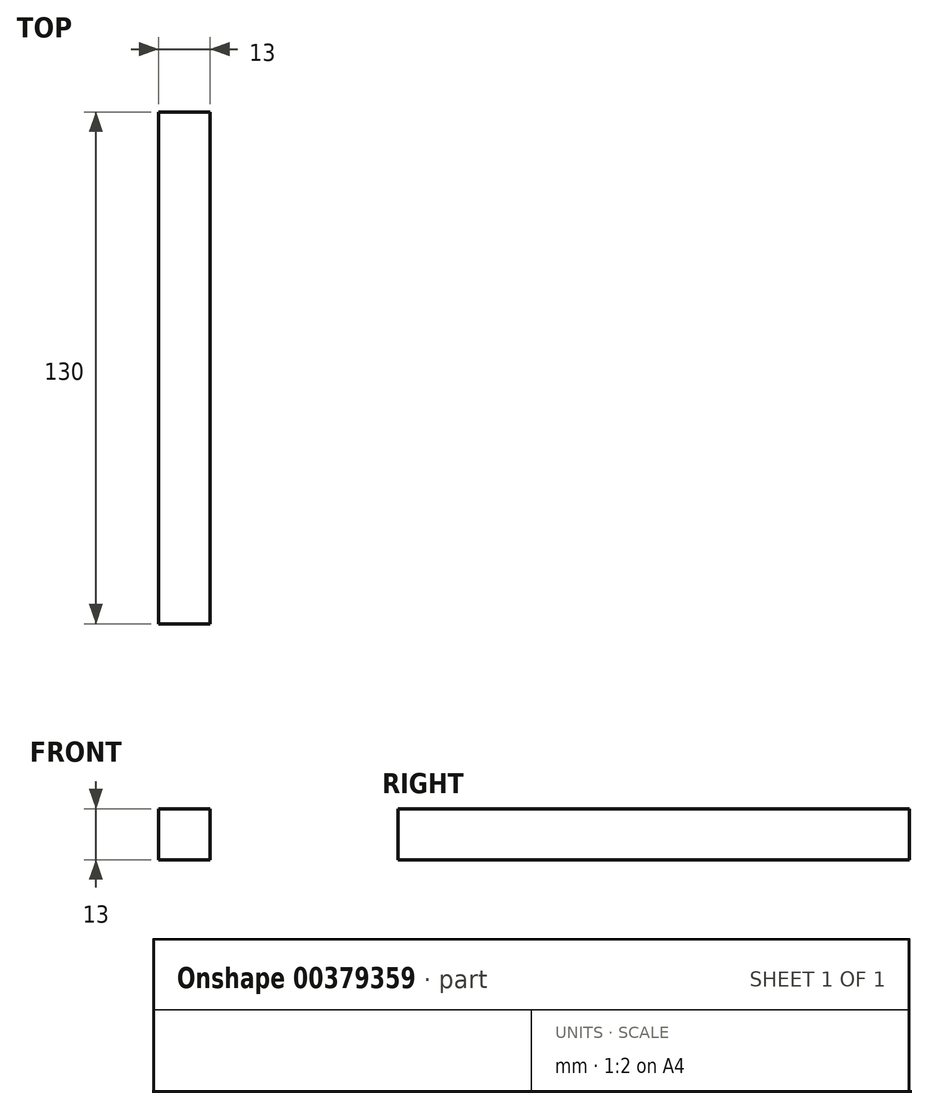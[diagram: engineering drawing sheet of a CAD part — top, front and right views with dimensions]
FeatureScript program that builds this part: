
annotation { "Feature Type Name" : "Feature", "Feature Type Description" : "" }
export const myFeature = defineFeature(function(context is Context, id is Id, definition is map)
    precondition{}
    {
        {
            var Q0;
            Q0=qCreatedBy(makeId("Front.planeOp"),FACE);
            var sketch = newSketch(context, id + "F0", { "sketchPlane" : qUnion([Q0])});
            skLineSegment(sketch, "E0.bottom", {"start": v(-45, 25.71) * mm, "end": v(-32, 25.71) * mm});
            skLineSegment(sketch, "E0.top", {"start": v(-45, 12.71) * mm, "end": v(-32, 12.71) * mm});
            skLineSegment(sketch, "E0.left", {"start": v(-45, 25.71) * mm, "end": v(-45, 12.71) * mm});
            skLineSegment(sketch, "E0.right", {"start": v(-32, 25.71) * mm, "end": v(-32, 12.71) * mm});
            skSolve(sketch);
        }
        {
            var Q0;
            Q0 = qSketchRegion(id + "F0", true);
            extrude(context, id + "F1", {"entities" : qUnion([Q0]), "depth" : 130 * mm, "offsetDistance" : 25 * mm});
        }
    });
